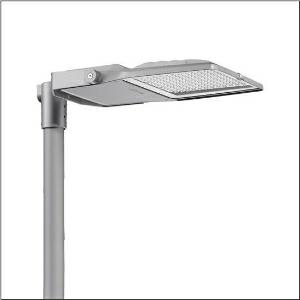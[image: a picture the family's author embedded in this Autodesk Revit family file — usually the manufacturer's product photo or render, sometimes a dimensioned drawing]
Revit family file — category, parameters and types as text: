
# Revit family: floodlight_fl_21_midi___pl61_5xa7781f2c3a_0da0
name_source: partatom
category: Lighting Fixtures
units: mm (PartAtom-declared; Revit-internal decimal feet)

## family parameters
Cut with Voids When Loaded = No
Host = Face
Light Source = No
Part Type = Normal
Room Calculation Point = No
Round Connector Dimension = Use Diameter
Shared = No

## types (1)
- --- (1 x LED, 35100 lm, 270.2 W, 3000K)
    Apparent Load = 270 VA
    CIE Flux Codes = 33 65 98 100 100
    Color Rendering = 70
    Color Temperature = 3000K
    Default Elevation = 1800 mm
    Description = Floodlight FL 21 midi, floodlight, primary light control with lens, of PMMA, primary optical cover: protective disc, of toughened safety glass, transparent, light distribution: PL61, light emission: direct distribution, installation type: surface-mounted, LED, High Power LED, rated luminous flux: 35.100lm, luminous efficacy: 129lm/W, light colour: 730, colour temperature: 3000K, control gear: ECG iQ, control: optimised constant luminous flux control (CLO 2.0), Desk-Remote (wireless, voltage-free reading and setting of iQ features in the workshop via application-optimized NFC function/RFID function), Light-Fading, Smart-Wire, Night-Set, Lumen-Switch, Temp-Guard, Auto-Match, with terminal, 6-pole, mains connection: 220..240V, AC, 50/60Hz, start of lifetime: 270W, end of lifetime: 286W, reduction: 129W, luminaire housing, of diecast aluminium, powder-coated, Siteco® metallic grey (DB 702S), corrosivity category C5 according to DIN EN ISO 12944, mast bracket, of steel, galvanised, powder-coated, Siteco® metallic grey (DB 702S), protection rating (complete): IP66, insulation class (complete): insulation class I (protective earthing), certification: CE, protection symbol: D, impact resistance: IK08, permissible operating ambient temperature: -40..+40°C, permissible operating ambient temperature for outdoor applications: -40..+50°C, standard: DIN EN 12944, packaging unit: 1 piece

Light Distribution: PL61
    Height = 76 mm
    Lamp = 1 x LED
    Lamp Light Flux = 35100 lm
    Lamp Power = 270.2 W
    Lamp count = 1
    Length = 657 mm
    Luminous efficacy = 130 lm/W
    Manufacturer = Siteco
    ModVariant = No
    Model = 5XA7781F2C3A
    Number of Poles = 1
    OnlyDefault = Yes
    Power Factor = 1
    Product Name = Floodlight FL 21 midi | PL61
    Product group = floodlight | pylon top
    ProductGroupID = 6101
    Protection Class = Protection class I
    Protection Degree = IP 66
    RLX_Detail_Level = 1
    RlxData = <blob elided: 153345 chars, md5=b181c240>
    Socket = socket
    Standby Power = 0 W
    System Light Flux = 35100 lm
    System Power = 270 W
    Type Comments = factory setting: luminous flux: 100 % | dim-lin: 254 | 620 mA
    Type Image = l_1007123.jpg
    URL = http://relux.com
    VarID = @adj_016967
    Voltage = 0 V
    Weight = 0.00 kg
    Width = 442 mm

## geometry (parser evidence)
native form markers: Blend x4, Sweep x11
no freeform markers — native parametric forms only
